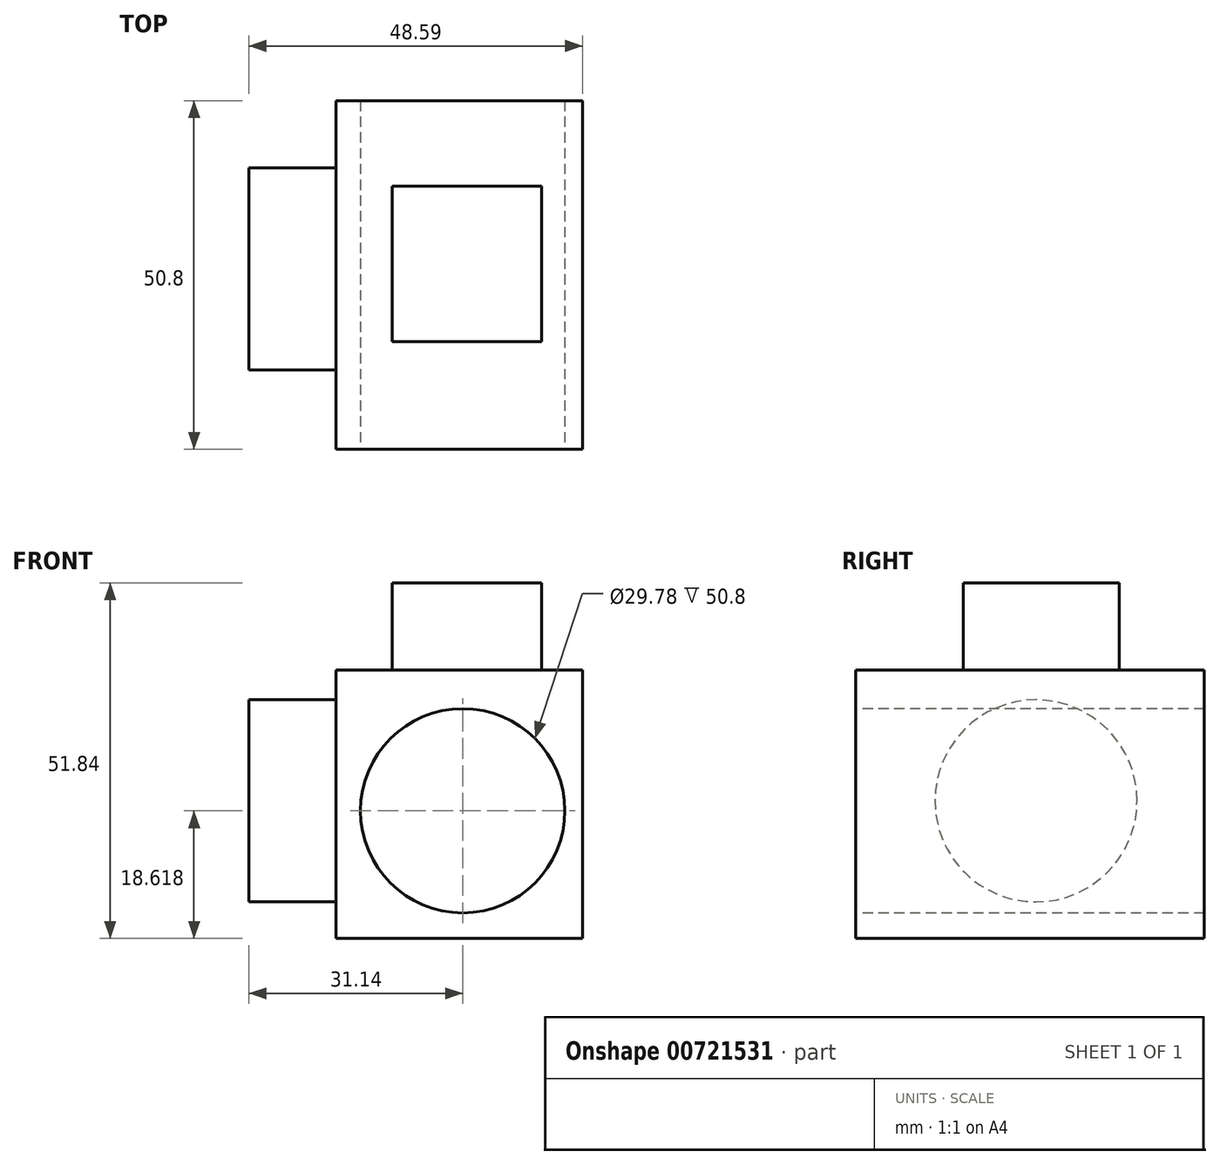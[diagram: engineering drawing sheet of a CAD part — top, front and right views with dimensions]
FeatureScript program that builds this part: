
annotation { "Feature Type Name" : "Feature", "Feature Type Description" : "" }
export const myFeature = defineFeature(function(context is Context, id is Id, definition is map)
    precondition{}
    {
        {
            var Q0;
            Q0=qCreatedBy(makeId("Front.planeOp"),FACE);
            var sketch = newSketch(context, id + "F0", { "sketchPlane" : qUnion([Q0])});
            skLineSegment(sketch, "E0", {"start": v(14.5, 39.14) * mm, "end": v(50.4, 39.14) * mm});
            skLineSegment(sketch, "E1", {"start": v(50.4, 39.14) * mm, "end": v(50.4, 0) * mm});
            skLineSegment(sketch, "E2", {"start": v(50.4, 0) * mm, "end": v(14.5, 0) * mm});
            skPoint(sketch, "E3.orphan", {"position": v(12.95, 39.14) * mm});
            skLineSegment(sketch, "E4", {"start": v(14.5, 39.14) * mm, "end": v(14.5, 0) * mm});
            skSolve(sketch);
        }
        {
            var Q0;
            Q0 = qSketchRegion(id + "F0", true);
            extrude(context, id + "F1", {"entities" : qUnion([Q0]), "depth" : 50.8 * mm, "offsetDistance" : 25.4 * mm});
        }
        {
            var Q0;
            Q0=makeQuery(id+"F1.opExtrude","CAP_FACE",FACE,{"disambiguationData":[OSD([sQuery(id+"F0.wireOp",EDGE,"E0"),sQuery(id+"F0.wireOp",EDGE,"E1"),sQuery(id+"F0.wireOp",EDGE,"E2"),sQuery(id+"F0.wireOp",EDGE,"E4")])],"isStart":false});
            var sketch = newSketch(context, id + "F2", { "sketchPlane" : qUnion([Q0])});
            skCircle(sketch, "E5", {"center": v(32.94, 18.62) * mm, "radius": 14.9 * mm});
            skSolve(sketch);
        }
        {
            var Q0;
            Q0 = qSketchRegion(id + "F2", true);
            extrude(context, id + "F3", {"entities" : qUnion([Q0]), "operationType" : NewBodyOperationType.REMOVE, "oppositeDirection" : true, "depth" : 50.8 * mm, "offsetDistance" : 25.4 * mm});
        }
        {
            var Q0;
            Q0=makeQuery(id+"F1.opExtrude","SWEPT_FACE",FACE,{"disambiguationData":[OSD([sQuery(id+"F0.wireOp",EDGE,"E4")])]});
            var sketch = newSketch(context, id + "F4", { "sketchPlane" : qUnion([Q0])});
            skCircle(sketch, "E6", {"center": v(24.54, 20.07) * mm, "radius": 14.73 * mm});
            skSolve(sketch);
        }
        {
            var Q0;
            Q0 = qSketchRegion(id + "F4", true);
            extrude(context, id + "F5", {"entities" : qUnion([Q0]), "operationType" : NewBodyOperationType.ADD, "depth" : 12.7 * mm, "offsetDistance" : 25.4 * mm});
        }
        {
            var Q0;
            Q0=makeQuery(id+"F1.opExtrude","SWEPT_FACE",FACE,{"disambiguationData":[OSD([sQuery(id+"F0.wireOp",EDGE,"E0")])]});
            var sketch = newSketch(context, id + "F6", { "sketchPlane" : qUnion([Q0])});
            skLineSegment(sketch, "E7.bottom", {"start": v(22.66, -12.43) * mm, "end": v(44.45, -12.43) * mm});
            skLineSegment(sketch, "E7.top", {"start": v(22.66, -35.13) * mm, "end": v(44.45, -35.13) * mm});
            skLineSegment(sketch, "E7.left", {"start": v(22.66, -12.43) * mm, "end": v(22.66, -35.13) * mm});
            skLineSegment(sketch, "E7.right", {"start": v(44.45, -12.43) * mm, "end": v(44.45, -35.13) * mm});
            skSolve(sketch);
        }
        {
            var Q0;
            Q0 = qSketchRegion(id + "F6", true);
            extrude(context, id + "F7", {"entities" : qUnion([Q0]), "operationType" : NewBodyOperationType.ADD, "depth" : 12.7 * mm, "offsetDistance" : 25.4 * mm});
        }
    });
